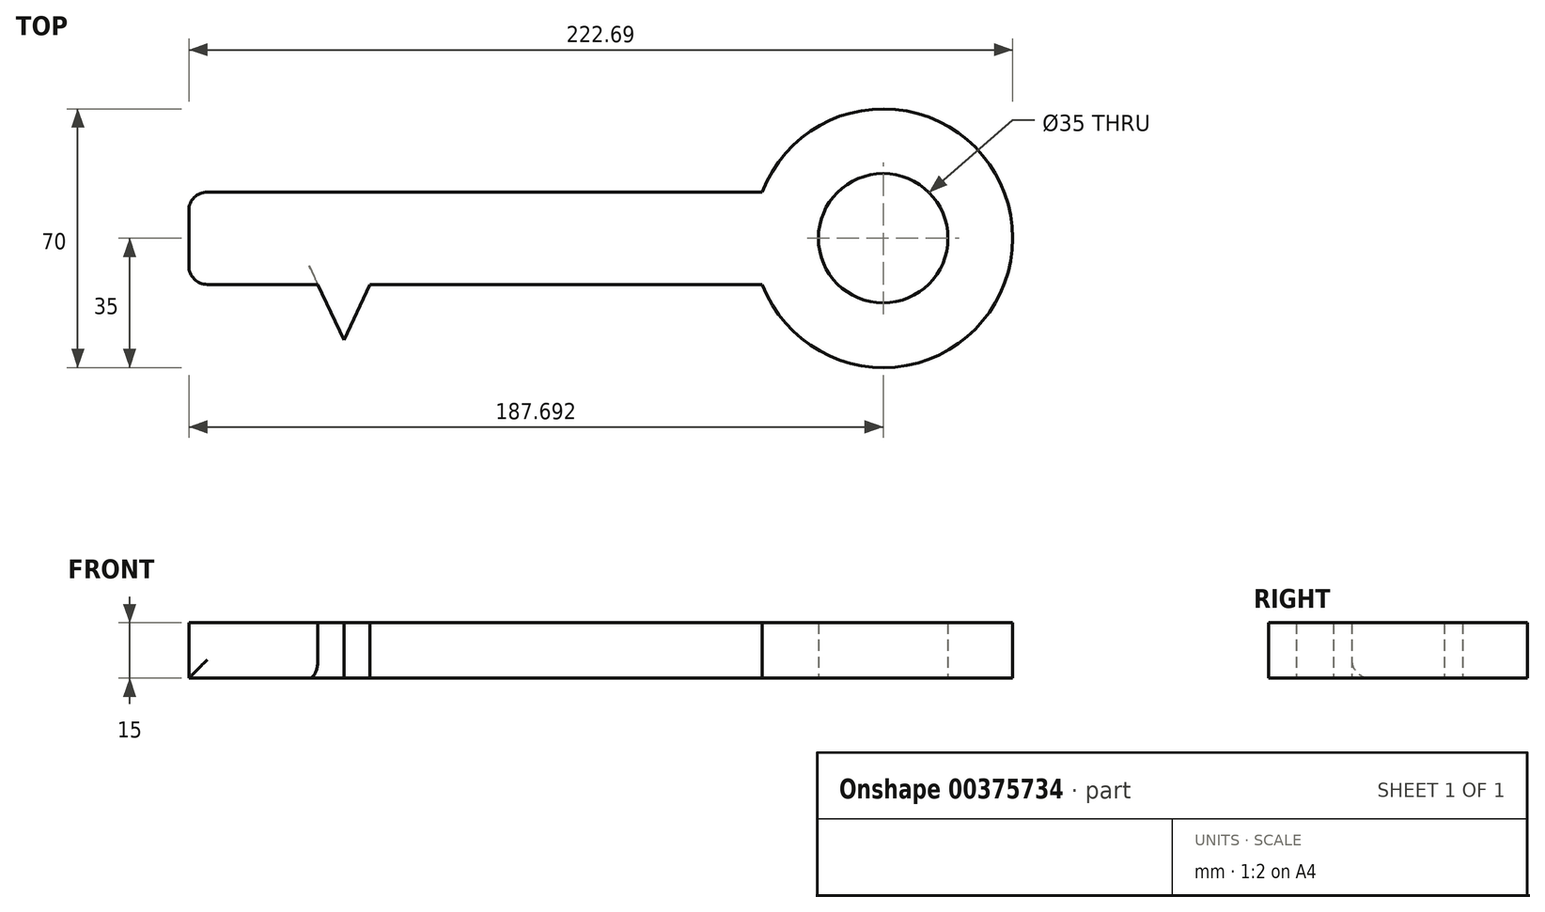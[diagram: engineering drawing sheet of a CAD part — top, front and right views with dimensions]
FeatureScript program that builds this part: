
annotation { "Feature Type Name" : "Feature", "Feature Type Description" : "" }
export const myFeature = defineFeature(function(context is Context, id is Id, definition is map)
    precondition{}
    {
        {
            var Q0;
            Q0=qCreatedBy(makeId("Top.planeOp"),FACE);
            var sketch = newSketch(context, id + "F0", { "sketchPlane" : qUnion([Q0])});
            skLineSegment(sketch, "E0.bottom", {"start": v(0, 0) * mm, "end": v(-155, 0) * mm});
            skLineSegment(sketch, "E0.top", {"start": v(0, 25) * mm, "end": v(-155, 25) * mm});
            skLineSegment(sketch, "E0.left", {"start": v(0, 0) * mm, "end": v(0, 25) * mm});
            skLineSegment(sketch, "E0.right", {"start": v(-155, 0) * mm, "end": v(-155, 25) * mm});
            skLineSegment(sketch, "E1.bottom", {"start": v(-155, 0) * mm, "end": v(-145, 0) * mm});
            skLineSegment(sketch, "E1.top", {"start": v(-155, -30) * mm, "end": v(-145, -30) * mm});
            skLineSegment(sketch, "E1.left", {"start": v(-155, 0) * mm, "end": v(-155, -30) * mm});
            skLineSegment(sketch, "E1.right", {"start": v(-145, 0) * mm, "end": v(-145, -30) * mm});
            skLineSegment(sketch, "E2.bottom", {"start": v(-135, 0) * mm, "end": v(-127, 0) * mm});
            skLineSegment(sketch, "E2.top", {"start": v(-135, -15) * mm, "end": v(-127, -15) * mm});
            skLineSegment(sketch, "E2.left", {"start": v(-135, 0) * mm, "end": v(-135, -15) * mm});
            skLineSegment(sketch, "E2.right", {"start": v(-127, 0) * mm, "end": v(-127, -15) * mm});
            skLineSegment(sketch, "E3", {"start": v(-120.1, 0) * mm, "end": v(-113.1, -15) * mm});
            skLineSegment(sketch, "E4", {"start": v(-106.1, 0) * mm, "end": v(-113.1, -15) * mm});
            skLineSegment(sketch, "E5", {"start": v(-120.1, 0) * mm, "end": v(-106.1, 0) * mm});
            skArc(sketch, "E6", {"start": v(0, 0) * mm, "mid": v(67.7, 12.5) * mm, "end": v(0, 25) * mm});
            skCircle(sketch, "E7", {"center": v(32.7, 12.5) * mm, "radius": 17.5 * mm});
            skLineSegment(sketch, "E8", {"start": v(32.7, 12.5) * mm, "end": v(-155, 12.5) * mm, "construction": true});
            skSolve(sketch);
        }
        {
            var Q0;
            Q0=makeQuery(id+"F0.imprint","IMPRINT",FACE,{"disambiguationData":[TD([[makeQuery(id+"F0.imprint","IMPRINT",EDGE,{"derivedFrom":sQuery(id+"F0.wireOp",EDGE,"E0.top")}),1.0]])]});
            var Q1;
            Q1=makeQuery(id+"F0.imprint","IMPRINT",FACE,{"disambiguationData":[TD([[makeQuery(id+"F0.imprint","IMPRINT",EDGE,{"derivedFrom":sQuery(id+"F0.wireOp",EDGE,"E0.left")}),-1.0]])]});
            var Q2;
            Q2=makeQuery(id+"F0.imprint","IMPRINT",FACE,{"disambiguationData":[TD([[makeQuery(id+"F0.imprint","IMPRINT",EDGE,{"derivedFrom":sQuery(id+"F0.wireOp",EDGE,"E3")}),1.0]])]});
            var Q3;
            Q3=makeQuery(id+"F0.imprint","IMPRINT",FACE,{"disambiguationData":[TD([[makeQuery(id+"F0.imprint","IMPRINT",EDGE,{"derivedFrom":sQuery(id+"F0.wireOp",EDGE,"E1.bottom")}),-1.0]])]});
            var Q4;
            Q4=makeQuery(id+"F0.imprint","IMPRINT",FACE,{"disambiguationData":[TD([[makeQuery(id+"F0.imprint","IMPRINT",EDGE,{"derivedFrom":sQuery(id+"F0.wireOp",EDGE,"E2.bottom")}),-1.0]])]});
            extrude(context, id + "F1", {"entities" : qUnion([Q0, Q1, Q2, Q3, Q4]), "depth" : 15 * mm});
        }
        {
            var Q0;
            Q0=makeQuery(id+"F1.opExtrude","SWEPT_EDGE",EDGE,{"disambiguationData":[OSD([sQuery(id+"F0.wireOp",EDGE,"E0.top"),sQuery(id+"F0.wireOp",EDGE,"E0.right")])]});
            var Q1;
            Q1=makeQuery(id+"F1.opExtrude","SWEPT_EDGE",EDGE,{"disambiguationData":[OSD([sQuery(id+"F0.wireOp",EDGE,"E1.top"),sQuery(id+"F0.wireOp",EDGE,"E1.left")])]});
            var Q2;
            Q2=makeQuery(id+"F1.opExtrude","CAP_EDGE",EDGE,{"disambiguationData":[OSD([sQuery(id+"F0.wireOp",EDGE,"E1.top")])],"isStart":false});
            var Q3;
            Q3=makeQuery(id+"F1.opExtrude","CAP_EDGE",EDGE,{"disambiguationData":[OSD([sQuery(id+"F0.wireOp",EDGE,"E1.right")])],"isStart":true});
            var Q4;
            {var subQ0=sQuery(id+"F0.wireOp",EDGE,"E0.bottom");Q4=makeQuery(id+"F1.opExtrude","CAP_EDGE",EDGE,{"disambiguationData":[OSD([subQ0]),TDD([makeQuery(id+"F0.imprint","IMPRINT",EDGE,{"disambiguationData":[TD([[makeQuery(id+"F0.imprint","INTERSECT",VERTEX,{"derivedFrom":[subQ0,sQuery(id+"F0.wireOp",EDGE,"E1.bottom"),sQuery(id+"F0.wireOp",EDGE,"E1.right")]}),1.0]])],"derivedFrom":subQ0})])],"isStart":true});}
            var Q5;
            Q5=makeQuery(id+"F1.opExtrude","CAP_EDGE",EDGE,{"disambiguationData":[OSD([sQuery(id+"F0.wireOp",EDGE,"E2.left")])],"isStart":true});
            var Q6;
            Q6=makeQuery(id+"F1.opExtrude","CAP_EDGE",EDGE,{"disambiguationData":[OSD([sQuery(id+"F0.wireOp",EDGE,"E2.top")])],"isStart":true});
            fillet(context, id + "F2", {"entities" : qUnion([Q0, Q1, Q2, Q3, Q4, Q5, Q6]), "radius" : 5 * mm, "tangentPropagation" : true, "allowEdgeOverflow" : false});
        }
    });
